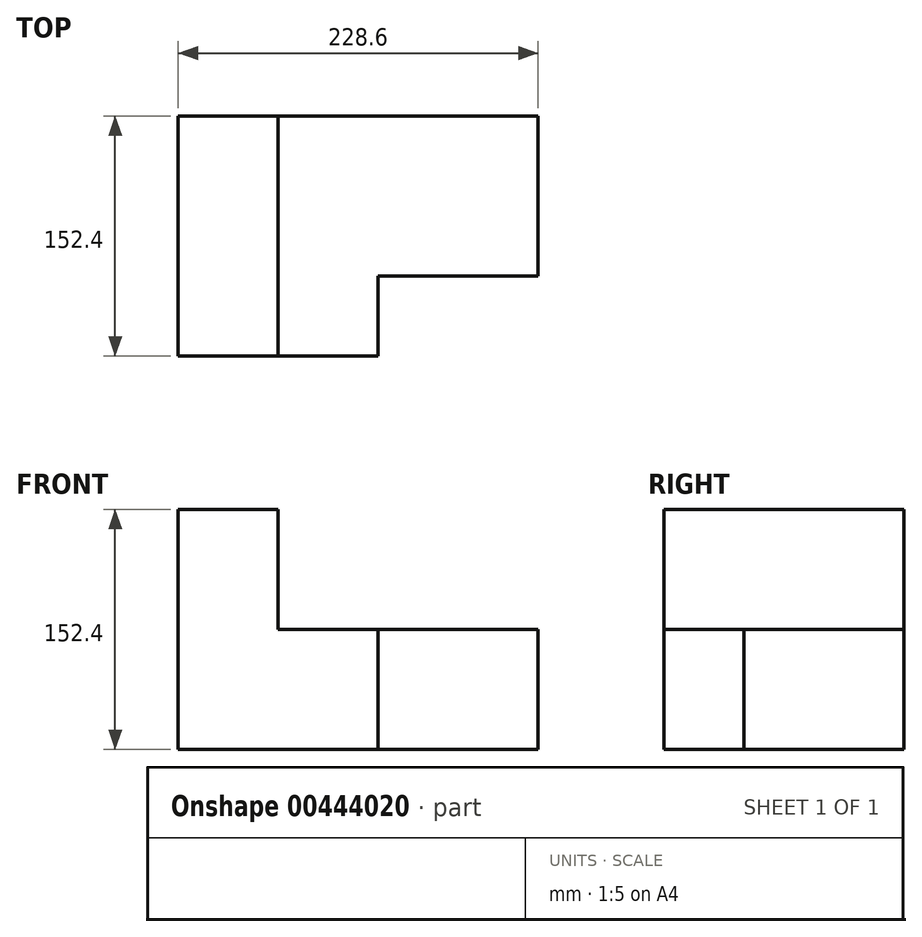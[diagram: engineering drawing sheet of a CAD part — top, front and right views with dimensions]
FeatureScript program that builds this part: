
annotation { "Feature Type Name" : "Feature", "Feature Type Description" : "" }
export const myFeature = defineFeature(function(context is Context, id is Id, definition is map)
    precondition{}
    {
        {
            var Q0;
            Q0=qCreatedBy(makeId("Front.planeOp"),FACE);
            var sketch = newSketch(context, id + "F0", { "sketchPlane" : qUnion([Q0])});
            skLineSegment(sketch, "E0", {"start": v(0, 0) * mm, "end": v(-228.6, 0) * mm});
            skLineSegment(sketch, "E1", {"start": v(-228.6, 0) * mm, "end": v(-228.6, 152.4) * mm});
            skLineSegment(sketch, "E2", {"start": v(-228.6, 152.4) * mm, "end": v(-165.1, 152.4) * mm});
            skLineSegment(sketch, "E3", {"start": v(-165.1, 152.4) * mm, "end": v(-165.1, 76.2) * mm});
            skLineSegment(sketch, "E4", {"start": v(-165.1, 76.2) * mm, "end": v(0, 76.2) * mm});
            skLineSegment(sketch, "E5", {"start": v(0, 76.2) * mm, "end": v(0, 0) * mm});
            skSolve(sketch);
        }
        {
            var Q0;
            Q0=makeQuery(id+"F0.imprint","IMPRINT",FACE,{"disambiguationData":[TD([[makeQuery(id+"F0.imprint","IMPRINT",EDGE,{"derivedFrom":sQuery(id+"F0.wireOp",EDGE,"E0")}),-1.0]])]});
            extrude(context, id + "F1", {"entities" : qUnion([Q0]), "endBound" : BoundingType.SYMMETRIC, "oppositeDirection" : true, "depth" : 152.4 * mm});
        }
        {
            var Q0;
            Q0=makeQuery(id+"F1.opExtrude","CAP_FACE",FACE,{"disambiguationData":[OSD([sQuery(id+"F0.wireOp",EDGE,"E0"),sQuery(id+"F0.wireOp",EDGE,"E1"),sQuery(id+"F0.wireOp",EDGE,"E2"),sQuery(id+"F0.wireOp",EDGE,"E3"),sQuery(id+"F0.wireOp",EDGE,"E4"),sQuery(id+"F0.wireOp",EDGE,"E5")])],"isStart":true});
            var sketch = newSketch(context, id + "F2", { "sketchPlane" : qUnion([Q0])});
            skLineSegment(sketch, "E6", {"start": v(0, 0) * mm, "end": v(-101.6, 0) * mm});
            skLineSegment(sketch, "E7", {"start": v(-101.6, 0) * mm, "end": v(-101.6, 76.2) * mm});
            skLineSegment(sketch, "E8", {"start": v(-101.6, 76.2) * mm, "end": v(0, 76.2) * mm});
            skLineSegment(sketch, "E9", {"start": v(0, 76.2) * mm, "end": v(0, 0) * mm});
            skSolve(sketch);
        }
        {
            var Q0;
            Q0=makeQuery(id+"F2.imprint","IMPRINT",FACE,{"disambiguationData":[TD([[makeQuery(id+"F2.imprint","IMPRINT",EDGE,{"derivedFrom":sQuery(id+"F2.wireOp",EDGE,"E6")}),-1.0]])]});
            extrude(context, id + "F3", {"entities" : qUnion([Q0]), "operationType" : NewBodyOperationType.REMOVE, "oppositeDirection" : true, "depth" : 50.8 * mm});
        }
    });
